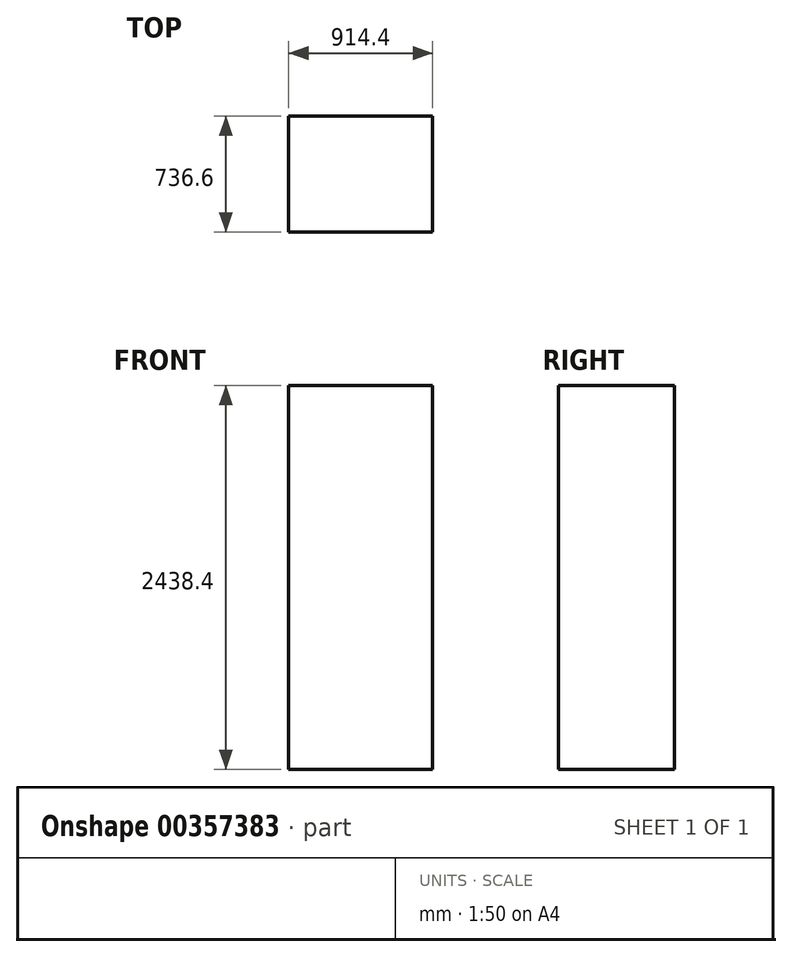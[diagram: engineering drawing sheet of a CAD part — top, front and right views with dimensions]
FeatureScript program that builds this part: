
annotation { "Feature Type Name" : "Feature", "Feature Type Description" : "" }
export const myFeature = defineFeature(function(context is Context, id is Id, definition is map)
    precondition{}
    {
        {
            var Q0;
            Q0=qCreatedBy(makeId("Top.planeOp"),FACE);
            var sketch = newSketch(context, id + "F0", { "sketchPlane" : qUnion([Q0])});
            skLineSegment(sketch, "E0.bottom", {"start": v(-457.2, -368.3) * mm, "end": v(457.2, -368.3) * mm});
            skLineSegment(sketch, "E0.top", {"start": v(-457.2, 368.3) * mm, "end": v(457.2, 368.3) * mm});
            skLineSegment(sketch, "E0.left", {"start": v(-457.2, -368.3) * mm, "end": v(-457.2, 368.3) * mm});
            skLineSegment(sketch, "E0.right", {"start": v(457.2, -368.3) * mm, "end": v(457.2, 368.3) * mm});
            skPoint(sketch, "E0.middle", {"position": v(0, 0) * mm});
            skSolve(sketch);
        }
        {
            var Q0;
            Q0 = qSketchRegion(id + "F0", true);
            extrude(context, id + "F1", {"entities" : qUnion([Q0]), "depth" : 2438.4 * mm});
        }
    });
